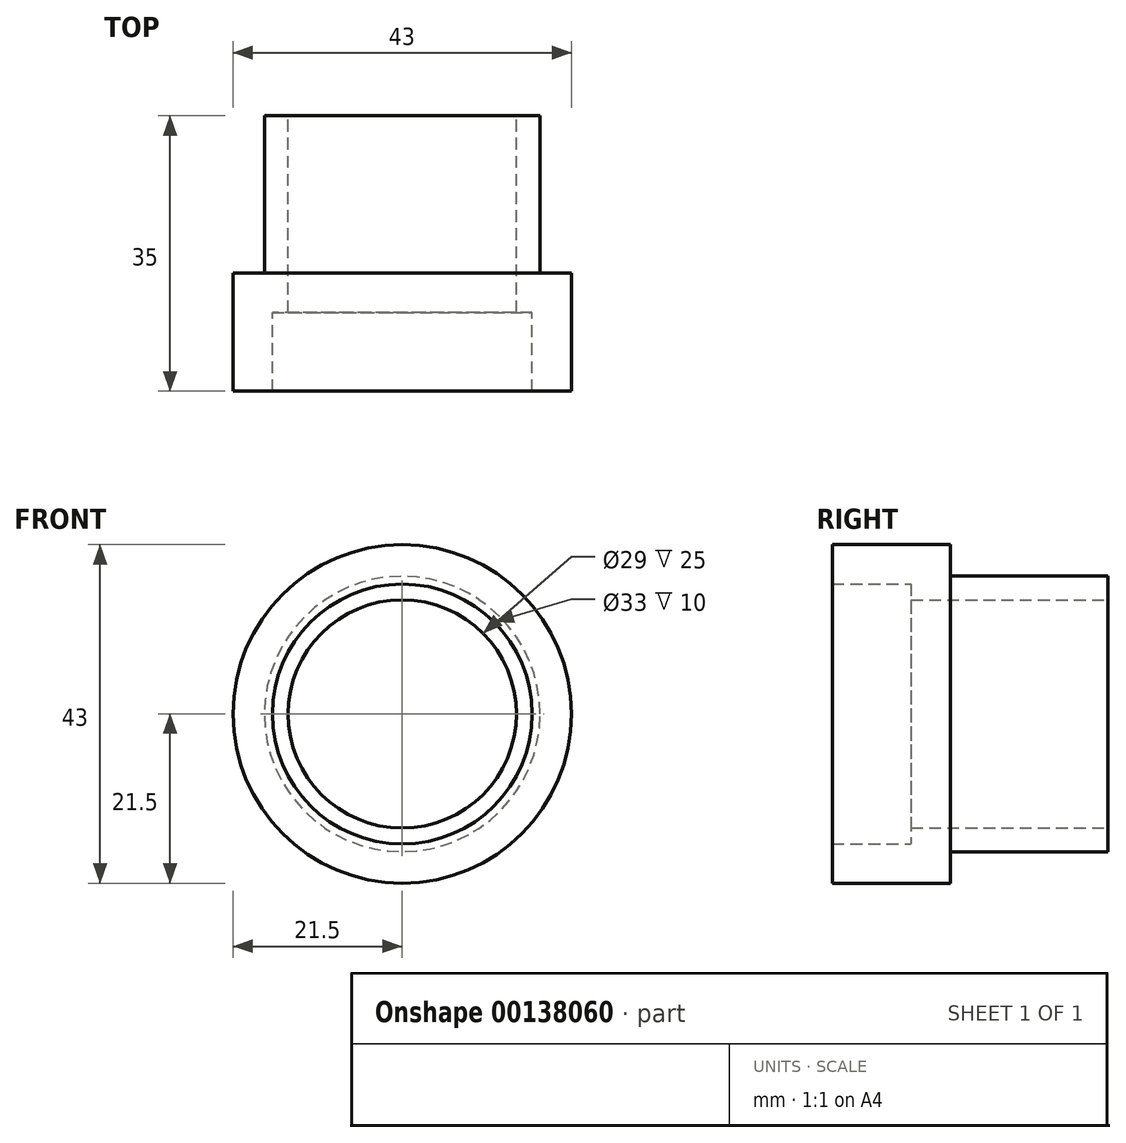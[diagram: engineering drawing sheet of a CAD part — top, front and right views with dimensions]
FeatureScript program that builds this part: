
annotation { "Feature Type Name" : "Feature", "Feature Type Description" : "" }
export const myFeature = defineFeature(function(context is Context, id is Id, definition is map)
    precondition{}
    {
        {
            var Q0;
            Q0=qCreatedBy(makeId("Top.planeOp"),FACE);
            var sketch = newSketch(context, id + "F0", { "sketchPlane" : qUnion([Q0])});
            skLineSegment(sketch, "E0", {"start": v(0, 33.86) * mm, "end": v(0, 0) * mm});
            skLineSegment(sketch, "E1", {"start": v(21.5, 0) * mm, "end": v(21.5, 15) * mm});
            skLineSegment(sketch, "E2", {"start": v(21.5, 15) * mm, "end": v(17.5, 15) * mm});
            skLineSegment(sketch, "E3", {"start": v(17.5, 15) * mm, "end": v(17.5, 35) * mm});
            skLineSegment(sketch, "E4", {"start": v(16.5, 0) * mm, "end": v(21.5, 0) * mm});
            skLineSegment(sketch, "E5", {"start": v(16.5, 0) * mm, "end": v(16.5, 10) * mm});
            skLineSegment(sketch, "E6", {"start": v(16.5, 10) * mm, "end": v(14.5, 10) * mm});
            skLineSegment(sketch, "E7", {"start": v(14.5, 10) * mm, "end": v(14.5, 35) * mm});
            skLineSegment(sketch, "E8", {"start": v(17.5, 35) * mm, "end": v(14.5, 35) * mm});
            skSolve(sketch);
        }
        {
            var Q0;
            Q0 = qSketchRegion(id + "F0", true);
            var Q1;
            Q1=sQuery(id+"F0.wireOp",EDGE,"E0");
            revolve(context, id + "F1", {"surfaceOperationType" : NewSurfaceOperationType.NEW, "entities" : qUnion([Q0]), "axis" : qUnion([Q1]), "revolveType" : RevolveType.FULL});
        }
    });
